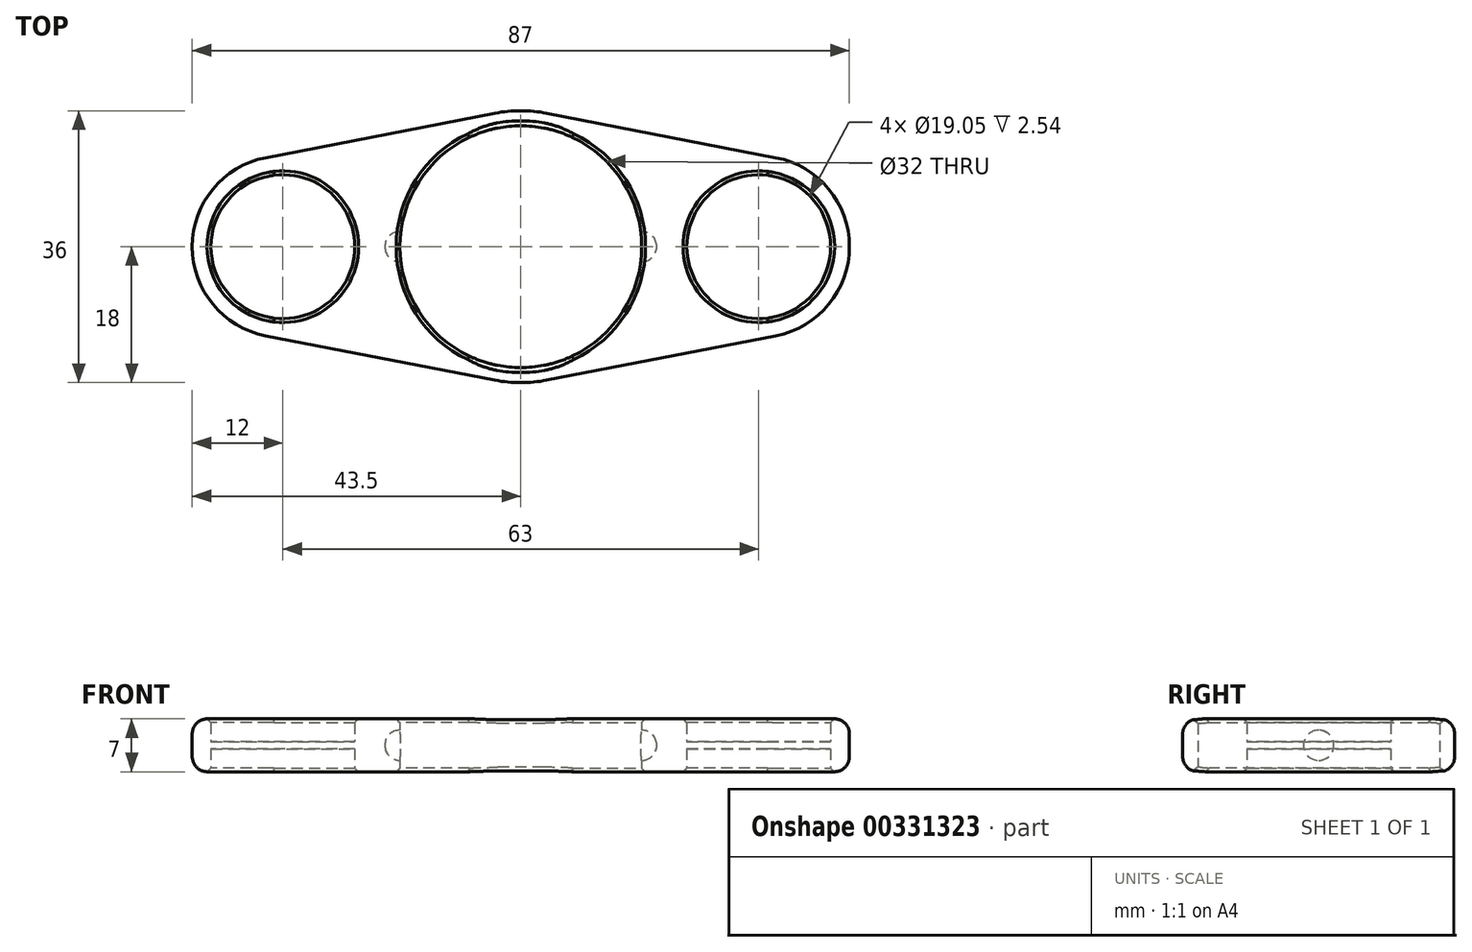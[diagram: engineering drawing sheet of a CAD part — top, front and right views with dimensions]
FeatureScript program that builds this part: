
annotation { "Feature Type Name" : "Feature", "Feature Type Description" : "" }
export const myFeature = defineFeature(function(context is Context, id is Id, definition is map)
    precondition{}
    {
        {
            var Q0;
            Q0=qCreatedBy(makeId("Top.planeOp"),FACE);
            var sketch = newSketch(context, id + "F0", { "sketchPlane" : qUnion([Q0])});
            skCircle(sketch, "E0", {"center": v(0, 0) * mm, "radius": 16 * mm});
            skArc(sketch, "E1", {"start": v(-3.43, -17.67) * mm, "mid": v(0, -18) * mm, "end": v(3.43, -17.67) * mm});
            skArc(sketch, "E2", {"start": v(33.79, -11.78) * mm, "mid": v(43.5, 0) * mm, "end": v(33.79, 11.78) * mm});
            skArc(sketch, "E3", {"start": v(-33.79, 11.78) * mm, "mid": v(-43.5, 0) * mm, "end": v(-33.79, -11.78) * mm});
            skLineSegment(sketch, "E4", {"start": v(-3.43, 17.67) * mm, "end": v(-33.79, 11.78) * mm});
            skLineSegment(sketch, "E5", {"start": v(-3.43, -17.67) * mm, "end": v(-33.79, -11.78) * mm});
            skLineSegment(sketch, "E6", {"start": v(3.43, 17.67) * mm, "end": v(33.79, 11.78) * mm});
            skLineSegment(sketch, "E7", {"start": v(33.79, -11.78) * mm, "end": v(3.43, -17.67) * mm});
            skArc(sketch, "E8.trimOffspring", {"start": v(3.43, 17.67) * mm, "mid": v(0, 18) * mm, "end": v(-3.43, 17.67) * mm});
            skCircle(sketch, "E9", {"center": v(0, 0) * mm, "radius": 43.5 * mm, "construction": true});
            skCircle(sketch, "E10", {"center": v(-31.5, 0) * mm, "radius": 9.53 * mm});
            skCircle(sketch, "E11", {"center": v(31.5, 0) * mm, "radius": 9.53 * mm});
            skSolve(sketch);
        }
        {
            var Q0;
            Q0=makeQuery(id+"F0.imprint","IMPRINT",FACE,{"disambiguationData":[TD([[makeQuery(id+"F0.imprint","IMPRINT",EDGE,{"derivedFrom":sQuery(id+"F0.wireOp",EDGE,"E0")}),-1.0]])]});
            extrude(context, id + "F1", {"entities" : qUnion([Q0]), "endBound" : BoundingType.SYMMETRIC, "depth" : 7 * mm, "offsetDistance" : 25 * mm});
        }
        {
            var Q0;
            Q0=makeQuery(id+"F1.opExtrude","CAP_EDGE",EDGE,{"disambiguationData":[OSD([sQuery(id+"F0.wireOp",EDGE,"E5")])],"isStart":false});
            var Q1;
            Q1=makeQuery(id+"F1.opExtrude","CAP_EDGE",EDGE,{"disambiguationData":[OSD([sQuery(id+"F0.wireOp",EDGE,"E5")])],"isStart":true});
            fillet(context, id + "F2", {"entities" : qUnion([Q0, Q1]), "radius" : 2 * mm, "tangentPropagation" : true, "allowEdgeOverflow" : false});
        }
        {
            var Q0;
            Q0=makeQuery(id+"F1.opExtrude","SWEPT_FACE",FACE,{"disambiguationData":[OSD([sQuery(id+"F0.wireOp",EDGE,"E0")])]});
            var Q1;
            Q1=makeQuery(id+"F1.opExtrude","CAP_EDGE",EDGE,{"disambiguationData":[OSD([sQuery(id+"F0.wireOp",EDGE,"E10")])],"isStart":false});
            var Q2;
            Q2=makeQuery(id+"F1.opExtrude","CAP_EDGE",EDGE,{"disambiguationData":[OSD([sQuery(id+"F0.wireOp",EDGE,"E10")])],"isStart":true});
            var Q3;
            Q3=makeQuery(id+"F1.opExtrude","CAP_EDGE",EDGE,{"disambiguationData":[OSD([sQuery(id+"F0.wireOp",EDGE,"E11")])],"isStart":false});
            var Q4;
            Q4=makeQuery(id+"F1.opExtrude","CAP_EDGE",EDGE,{"disambiguationData":[OSD([sQuery(id+"F0.wireOp",EDGE,"E11")])],"isStart":true});
            chamfer(context, id + "F3", {"entities" : qUnion([Q0, Q1, Q2, Q3, Q4]), "width" : .5 * mm, "tangentPropagation" : true});
        }
        {
            var Q0;
            Q0=qCreatedBy(makeId("Right.planeOp"),FACE);
            var sketch = newSketch(context, id + "F4", { "sketchPlane" : qUnion([Q0])});
            skCircle(sketch, "E12", {"center": v(0, 0) * mm, "radius": 2 * mm});
            skLineSegment(sketch, "E13", {"start": v(0, 0) * mm, "end": v(0, 0) * mm});
            skSolve(sketch);
        }
        {
            var Q0;
            Q0 = qSketchRegion(id + "F4", true);
            extrude(context, id + "F5", {"entities" : qUnion([Q0]), "operationType" : NewBodyOperationType.REMOVE, "endBound" : BoundingType.SYMMETRIC, "depth" : 36 * mm});
        }
        {
            var Q0;
            Q0=makeQuery(id+"F5.boolean.opBoolean","COPY",EDGE,{"derivedFrom":makeQuery(id+"F5.opExtrude","CAP_EDGE",EDGE,{"disambiguationData":[OSD([sQuery(id+"F4.wireOp",EDGE,"E12")])],"isStart":false})});
            var Q1;
            Q1=makeQuery(id+"F5.boolean.opBoolean","COPY",EDGE,{"derivedFrom":makeQuery(id+"F5.opExtrude","CAP_EDGE",EDGE,{"disambiguationData":[OSD([sQuery(id+"F4.wireOp",EDGE,"E12")])],"isStart":true})});
            fillet(context, id + "F6", {"entities" : qUnion([Q0, Q1]), "radius" : 2 * mm, "tangentPropagation" : true, "allowEdgeOverflow" : false});
        }
        {
            var Q0;
            Q0=qCreatedBy(makeId("Top.planeOp"),FACE);
            var sketch = newSketch(context, id + "F7", { "sketchPlane" : qUnion([Q0])});
            skArc(sketch, "E14.0", {"start": v(32.65, 9.46) * mm, "mid": v(21.98, 0) * mm, "end": v(32.65, -9.46) * mm});
            skArc(sketch, "E15.0", {"start": v(33.31, -9.35) * mm, "mid": v(41.02, 0) * mm, "end": v(33.31, 9.35) * mm});
            skArc(sketch, "E16.0", {"start": v(32.65, 9.46) * mm, "mid": v(32.98, 9.4) * mm, "end": v(33.31, 9.35) * mm});
            skArc(sketch, "E17.0", {"start": v(33.31, -9.35) * mm, "mid": v(32.98, -9.4) * mm, "end": v(32.65, -9.46) * mm});
            skArc(sketch, "E18.0", {"start": v(-32.65, -9.46) * mm, "mid": v(-21.98, 0) * mm, "end": v(-32.65, 9.46) * mm});
            skPoint(sketch, "E19.0", {"position": v(-32.98, 9.4) * mm});
            skArc(sketch, "E20.0", {"start": v(-33.31, 9.35) * mm, "mid": v(-41.02, 0) * mm, "end": v(-33.31, -9.35) * mm});
            skArc(sketch, "E21.0", {"start": v(-33.31, 9.35) * mm, "mid": v(-32.98, 9.4) * mm, "end": v(-32.65, 9.46) * mm});
            skArc(sketch, "E22.0", {"start": v(-32.65, -9.46) * mm, "mid": v(-32.98, -9.4) * mm, "end": v(-33.31, -9.35) * mm});
            skSolve(sketch);
        }
        {
            var Q0;
            Q0=makeQuery(id+"F7.imprint","IMPRINT",FACE,{"disambiguationData":[TD([[makeQuery(id+"F7.imprint","IMPRINT",EDGE,{"derivedFrom":sQuery(id+"F7.wireOp",EDGE,"E18.0")}),1.0]])]});
            var Q1;
            Q1=makeQuery(id+"F7.imprint","IMPRINT",FACE,{"disambiguationData":[TD([[makeQuery(id+"F7.imprint","IMPRINT",EDGE,{"derivedFrom":sQuery(id+"F7.wireOp",EDGE,"E14.0")}),1.0]])]});
            extrude(context, id + "F8", {"entities" : qUnion([Q0, Q1]), "operationType" : NewBodyOperationType.ADD, "endBound" : BoundingType.SYMMETRIC, "depth" : .920 * mm, "offsetDistance" : 25 * mm});
        }
    });
